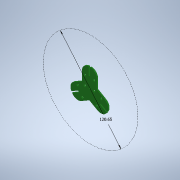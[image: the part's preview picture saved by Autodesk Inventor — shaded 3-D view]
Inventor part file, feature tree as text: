
AUTODESK INVENTOR PART (.ipt)
format: ipt  version: 2021 (Build 250183000, 183)  size: 139,264 bytes
history: native  units: in
note: dims shown in document units (in); Inventor stores cm internally (conversion verified against a paired STEP export)
features: imported_body x1, sketch x1
ambient origin geometry x8: Origin, YZ Plane, XZ Plane, XY Plane, X Axis, Y Axis, Z Axis, Center Point
bodies: Solid1 (feature_tree)
feature tree (2):
  imported_body  "Base1"
  sketch  "Sketch1"  dims[d0=4.75in]
